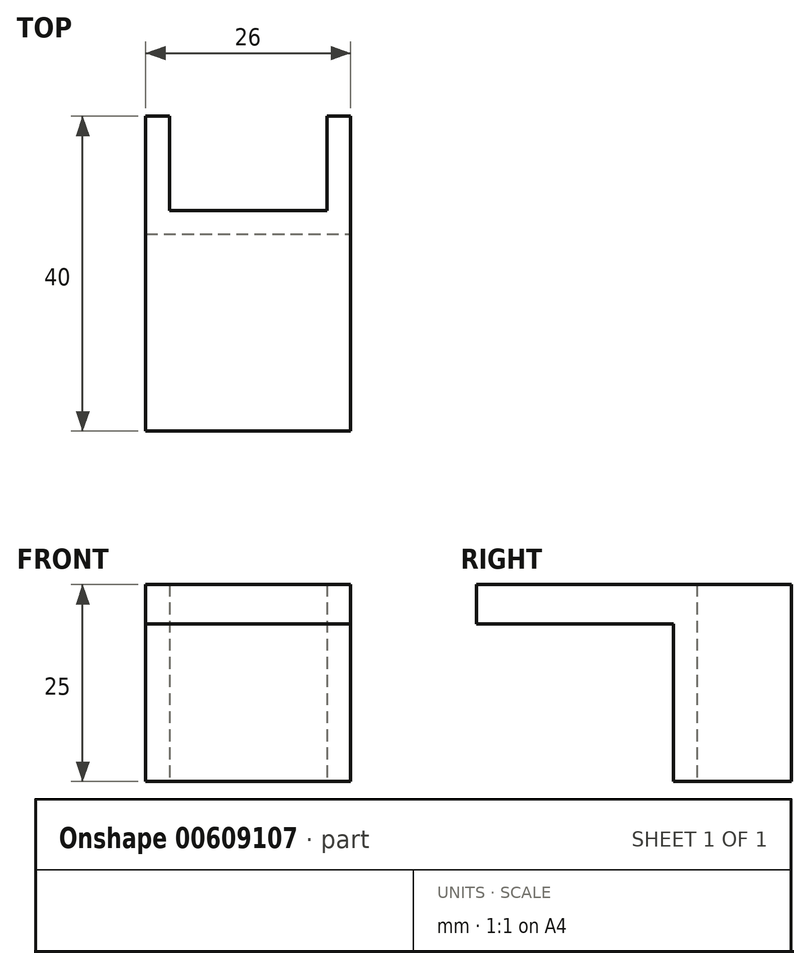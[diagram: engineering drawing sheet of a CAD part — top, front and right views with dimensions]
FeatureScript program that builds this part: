
annotation { "Feature Type Name" : "Feature", "Feature Type Description" : "" }
export const myFeature = defineFeature(function(context is Context, id is Id, definition is map)
    precondition{}
    {
        {
            var Q0;
            Q0=qCreatedBy(makeId("Top.planeOp"),FACE);
            var sketch = newSketch(context, id + "F0", { "sketchPlane" : qUnion([Q0])});
            skLineSegment(sketch, "E0.bottom", {"start": v(-13, 7.5) * mm, "end": v(13, 7.5) * mm});
            skLineSegment(sketch, "E0.top", {"start": v(-13, -7.5) * mm, "end": v(13, -7.5) * mm});
            skLineSegment(sketch, "E0.left", {"start": v(-13, 7.5) * mm, "end": v(-13, -7.5) * mm});
            skLineSegment(sketch, "E0.right", {"start": v(13, 7.5) * mm, "end": v(13, -7.5) * mm});
            skPoint(sketch, "E0.middle", {"position": v(0, 0) * mm});
            skLineSegment(sketch, "E1.bottom", {"start": v(-10, 10.5) * mm, "end": v(10, 10.5) * mm});
            skLineSegment(sketch, "E1.top", {"start": v(-10, -4.5) * mm, "end": v(10, -4.5) * mm});
            skLineSegment(sketch, "E1.left", {"start": v(-10, 10.5) * mm, "end": v(-10, -4.5) * mm});
            skLineSegment(sketch, "E1.right", {"start": v(10, 10.5) * mm, "end": v(10, -4.5) * mm});
            skSolve(sketch);
        }
        {
            var Q0;
            Q0=makeQuery(id+"F0.imprint","IMPRINT",FACE,{"disambiguationData":[TD([[makeQuery(id+"F0.imprint","IMPRINT",EDGE,{"derivedFrom":sQuery(id+"F0.wireOp",EDGE,"E0.top")}),1.0]])]});
            extrude(context, id + "F1", {"entities" : qUnion([Q0]), "depth" : 25 * mm});
        }
        {
            var Q0;
            Q0=makeQuery(id+"F1.opExtrude","SWEPT_FACE",FACE,{"disambiguationData":[OSD([sQuery(id+"F0.wireOp",EDGE,"E0.top")])]});
            var sketch = newSketch(context, id + "F2", { "sketchPlane" : qUnion([Q0])});
            skLineSegment(sketch, "E2.bottom", {"start": v(-13, 25) * mm, "end": v(13, 25) * mm});
            skLineSegment(sketch, "E2.top", {"start": v(-13, 20) * mm, "end": v(13, 20) * mm});
            skLineSegment(sketch, "E2.left", {"start": v(-13, 25) * mm, "end": v(-13, 20) * mm});
            skLineSegment(sketch, "E2.right", {"start": v(13, 25) * mm, "end": v(13, 20) * mm});
            skSolve(sketch);
        }
        {
            var Q0;
            Q0=makeQuery(id+"F2.imprint","IMPRINT",FACE,{"disambiguationData":[TD([[makeQuery(id+"F2.imprint","IMPRINT",EDGE,{"derivedFrom":sQuery(id+"F2.wireOp",EDGE,"E2.bottom")}),-1.0]])]});
            extrude(context, id + "F3", {"entities" : qUnion([Q0]), "operationType" : NewBodyOperationType.ADD, "depth" : 25 * mm});
        }
    });
